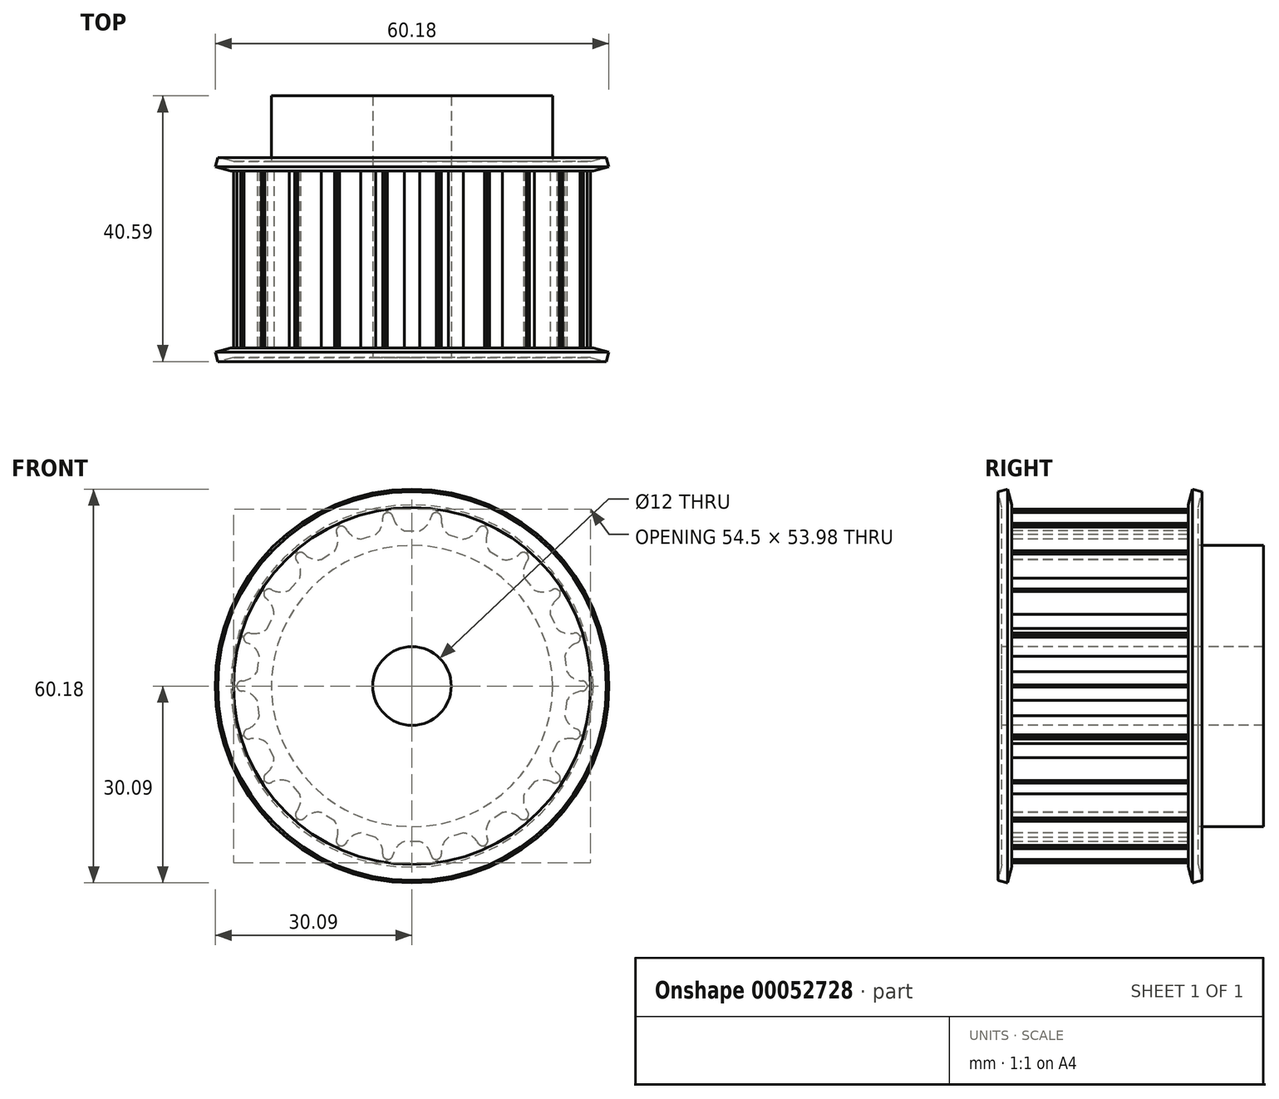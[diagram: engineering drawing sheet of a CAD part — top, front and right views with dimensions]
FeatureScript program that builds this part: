
annotation { "Feature Type Name" : "Feature", "Feature Type Description" : "" }
export const myFeature = defineFeature(function(context is Context, id is Id, definition is map)
    precondition{}
    {
        {
            var Q0;
            Q0=qCreatedBy(makeId("Right.planeOp"),FACE);
            var sketch = newSketch(context, id + "F0", { "sketchPlane" : qUnion([Q0])});
            skLineSegment(sketch, "E0", {"start": v(-51.89, 0) * mm, "end": v(51.76, 0) * mm, "construction": true});
            skLineSegment(sketch, "E1", {"start": v(0, 6) * mm, "end": v(0, 27.25) * mm});
            skLineSegment(sketch, "E2", {"start": v(0, 27.25) * mm, "end": v(30, 27.25) * mm});
            skLineSegment(sketch, "E3", {"start": v(30, 27.25) * mm, "end": v(30, 21.5) * mm});
            skLineSegment(sketch, "E4", {"start": v(30, 21.5) * mm, "end": v(40, 21.5) * mm});
            skLineSegment(sketch, "E5", {"start": v(40, 21.5) * mm, "end": v(40, 6) * mm});
            skLineSegment(sketch, "E6", {"start": v(40, 6) * mm, "end": v(0, 6) * mm});
            skSolve(sketch);
        }
        {
            var Q0;
            Q0=makeQuery(id+"F0.imprint","IMPRINT",FACE,{"disambiguationData":[TD([[makeQuery(id+"F0.imprint","IMPRINT",EDGE,{"derivedFrom":sQuery(id+"F0.wireOp",EDGE,"E1")}),-1.0]])]});
            var Q1;
            Q1=sQuery(id+"F0.wireOp",EDGE,"E0");
            revolve(context, id + "F1", {"entities" : qUnion([Q0]), "axis" : qUnion([Q1]), "revolveType" : RevolveType.FULL});
        }
        {
            var Q0;
            Q0=makeQuery(id+"F1.opRevolve","SWEPT_FACE",FACE,{"disambiguationData":[OSD([sQuery(id+"F0.wireOp",EDGE,"E1")])]});
            var sketch = newSketch(context, id + "F2", { "sketchPlane" : qUnion([Q0])});
            skArc(sketch, "E7", {"start": v(-2.94, 25.9) * mm, "mid": v(0, 23.5) * mm, "end": v(2.94, 25.9) * mm});
            skLineSegment(sketch, "E8.rect.bottom", {"start": v(-3.75, 28.5) * mm, "end": v(3.75, 28.5) * mm});
            skLineSegment(sketch, "E8.rect.top", {"start": v(-3.75, 26.5) * mm, "end": v(-3.67, 26.5) * mm});
            skLineSegment(sketch, "E8.rect.left", {"start": v(-3.75, 28.5) * mm, "end": v(-3.75, 26.5) * mm});
            skLineSegment(sketch, "E8.rect.right", {"start": v(3.75, 28.5) * mm, "end": v(3.75, 26.5) * mm});
            skPoint(sketch, "E8.rect.middle", {"position": v(0, 27.5) * mm});
            skLineSegment(sketch, "E9.trimOffspring", {"start": v(3.67, 26.5) * mm, "end": v(3.75, 26.5) * mm});
            skPoint(sketch, "E10.visualSharp", {"position": v(-3, 26.5) * mm});
            skArc(sketch, "E10.filletArc", {"start": v(-2.94, 25.9) * mm, "mid": v(-3.2, 26.33) * mm, "end": v(-3.67, 26.5) * mm});
            skPoint(sketch, "E11.visualSharp", {"position": v(3, 26.5) * mm});
            skArc(sketch, "E11.filletArc", {"start": v(3.67, 26.5) * mm, "mid": v(3.2, 26.33) * mm, "end": v(2.94, 25.9) * mm});
            skLineSegment(sketch, "E12", {"start": v(-1.2, 23.75) * mm, "end": v(1.2, 23.75) * mm});
            skPoint(sketch, "E13", {"position": v(0, 23.75) * mm});
            skSolve(sketch);
        }
        {
            var Q0;
            {var subQ0=sQuery(id+"F2.wireOp",EDGE,"E8.rect.bottom");Q0=makeQuery(id+"F2.imprint","IMPRINT",FACE,{"disambiguationData":[TD([[makeQuery(id+"F2.imprint","IMPRINT",EDGE,{"derivedFrom":subQ0}),-1.0]])]});}
            var Q1;
            Q1=makeQuery(id+"F2.imprint","IMPRINT",FACE,{"disambiguationData":[TD([[makeQuery(id+"F2.imprint","IMPRINT",EDGE,{"derivedFrom":sQuery(id+"F2.wireOp",EDGE,"E7")}),1.0]])]});
            var Q2;
            Q2=makeQuery(id+"F1.opRevolve","SWEPT_FACE",FACE,{"disambiguationData":[OSD([sQuery(id+"F0.wireOp",EDGE,"E3")])]});
            extrude(context, id + "F3", {"entities" : qUnion([Q0, Q1]), "endBound" : BoundingType.THROUGH_ALL, "oppositeDirection" : true, "endBoundEntityFace" : qUnion([Q2]), "depth" : 25 * mm});
        }
        {
            var Q0;
            Q0=makeQuery(id+"F3.opExtrude","SWEPT_BODY",BODY,{"disambiguationData":[OSD([sQuery(id+"F2.wireOp",EDGE,"E7"),sQuery(id+"F2.wireOp",EDGE,"E8.rect.bottom"),sQuery(id+"F2.wireOp",EDGE,"E8.rect.top"),sQuery(id+"F2.wireOp",EDGE,"E8.rect.left"),sQuery(id+"F2.wireOp",EDGE,"E8.rect.right"),sQuery(id+"F2.wireOp",EDGE,"E9.trimOffspring"),sQuery(id+"F2.wireOp",EDGE,"E10.filletArc"),sQuery(id+"F2.wireOp",EDGE,"E11.filletArc"),sQuery(id+"F2.wireOp",EDGE,"E12")])]});
            var Q1;
            Q1=sQuery(id+"F0.wireOp",EDGE,"E0");
            circularPattern(context, id + "F4", {"operationType" : NewBodyOperationType.REMOVE, "entities" : qUnion([Q0]), "axis" : qUnion([Q1]), "angle" : 360 * degree, "instanceCount" : round(22), "equalSpace" : true});
        }
        {
            var Q0;
            Q0=qCreatedBy(makeId("Right.planeOp"),FACE);
            var sketch = newSketch(context, id + "F5", { "sketchPlane" : qUnion([Q0])});
            skLineSegment(sketch, "E14", {"start": v(0, 0) * mm, "end": v(15, 0) * mm, "construction": true});
            skLineSegment(sketch, "E15", {"start": v(15, 0) * mm, "end": v(15, -79.13) * mm, "construction": true});
            skLineSegment(sketch, "E16", {"start": v(0, 23.75) * mm, "end": v(1.5, 23.75) * mm});
            skLineSegment(sketch, "E17", {"start": v(0, 23.75) * mm, "end": v(0, 27.7) * mm});
            skLineSegment(sketch, "E18", {"start": v(0, 27.7) * mm, "end": v(1.5, 27.7) * mm});
            skLineSegment(sketch, "E19", {"start": v(1.5, 27.7) * mm, "end": v(1.5, 23.75) * mm});
            skLineSegment(sketch, "E20", {"start": v(1.5, 27.7) * mm, "end": v(0.86, 30.1) * mm});
            skLineSegment(sketch, "E21", {"start": v(1.5, 27.7) * mm, "end": v(0, 27.29) * mm});
            skLineSegment(sketch, "E22", {"start": v(0.86, 30.1) * mm, "end": v(-0.6, 29.7) * mm});
            skLineSegment(sketch, "E23", {"start": v(-0.6, 29.7) * mm, "end": v(0, 27.29) * mm});
            skLineSegment(sketch, "E24", {"start": v(15, 0) * mm, "end": v(15, 84.63) * mm, "construction": true});
            skLineSegment(sketch, "E25.MirrorCS", {"start": v(30, 27.7) * mm, "end": v(28.5, 27.7) * mm});
            skLineSegment(sketch, "E26.MirrorCS", {"start": v(28.5, 27.7) * mm, "end": v(30, 27.29) * mm});
            skLineSegment(sketch, "E27.MirrorCS", {"start": v(30.6, 29.7) * mm, "end": v(30, 27.29) * mm});
            skLineSegment(sketch, "E28.MirrorCS", {"start": v(29.14, 30.1) * mm, "end": v(30.6, 29.7) * mm});
            skLineSegment(sketch, "E29.MirrorCS", {"start": v(30, 23.75) * mm, "end": v(28.5, 23.75) * mm});
            skLineSegment(sketch, "E30.MirrorCS", {"start": v(28.5, 27.7) * mm, "end": v(29.14, 30.1) * mm});
            skLineSegment(sketch, "E31.MirrorCS", {"start": v(30, 23.75) * mm, "end": v(30, 27.7) * mm});
            skLineSegment(sketch, "E32.MirrorCS", {"start": v(28.5, 27.7) * mm, "end": v(28.5, 23.75) * mm});
            skSolve(sketch);
        }
        {
            var Q0;
            {var subQ1=sQuery(id+"F5.wireOp",EDGE,"E18");Q0=makeQuery(id+"F5.imprint","IMPRINT",FACE,{"disambiguationData":[TD([[makeQuery(id+"F5.imprint","IMPRINT",EDGE,{"derivedFrom":subQ1}),1.0]])]});}
            var Q1;
            {var subQ0=sQuery(id+"F5.wireOp",EDGE,"E18");Q1=makeQuery(id+"F5.imprint","IMPRINT",FACE,{"disambiguationData":[TD([[makeQuery(id+"F5.imprint","IMPRINT",EDGE,{"derivedFrom":subQ0}),-1.0]])]});}
            var Q2;
            {var subQ0=sQuery(id+"F5.wireOp",EDGE,"E16");Q2=makeQuery(id+"F5.imprint","IMPRINT",FACE,{"disambiguationData":[TD([[makeQuery(id+"F5.imprint","IMPRINT",EDGE,{"derivedFrom":subQ0}),1.0]])]});}
            var Q3;
            {var subQ1=sQuery(id+"F5.wireOp",EDGE,"E25.MirrorCS");Q3=makeQuery(id+"F5.imprint","IMPRINT",FACE,{"disambiguationData":[TD([[makeQuery(id+"F5.imprint","IMPRINT",EDGE,{"derivedFrom":subQ1}),-1.0]])]});}
            var Q4;
            {var subQ0=sQuery(id+"F5.wireOp",EDGE,"E25.MirrorCS");Q4=makeQuery(id+"F5.imprint","IMPRINT",FACE,{"disambiguationData":[TD([[makeQuery(id+"F5.imprint","IMPRINT",EDGE,{"derivedFrom":subQ0}),1.0]])]});}
            var Q5;
            {var subQ0=sQuery(id+"F5.wireOp",EDGE,"E26.MirrorCS");Q5=makeQuery(id+"F5.imprint","IMPRINT",FACE,{"disambiguationData":[TD([[makeQuery(id+"F5.imprint","IMPRINT",EDGE,{"derivedFrom":subQ0}),-1.0]])]});}
            var Q6;
            Q6=sQuery(id+"F0.wireOp",EDGE,"E0");
            revolve(context, id + "F6", {"operationType" : NewBodyOperationType.ADD, "entities" : qUnion([Q0, Q1, Q2, Q3, Q4, Q5]), "axis" : qUnion([Q6]), "revolveType" : RevolveType.FULL});
        }
    });
